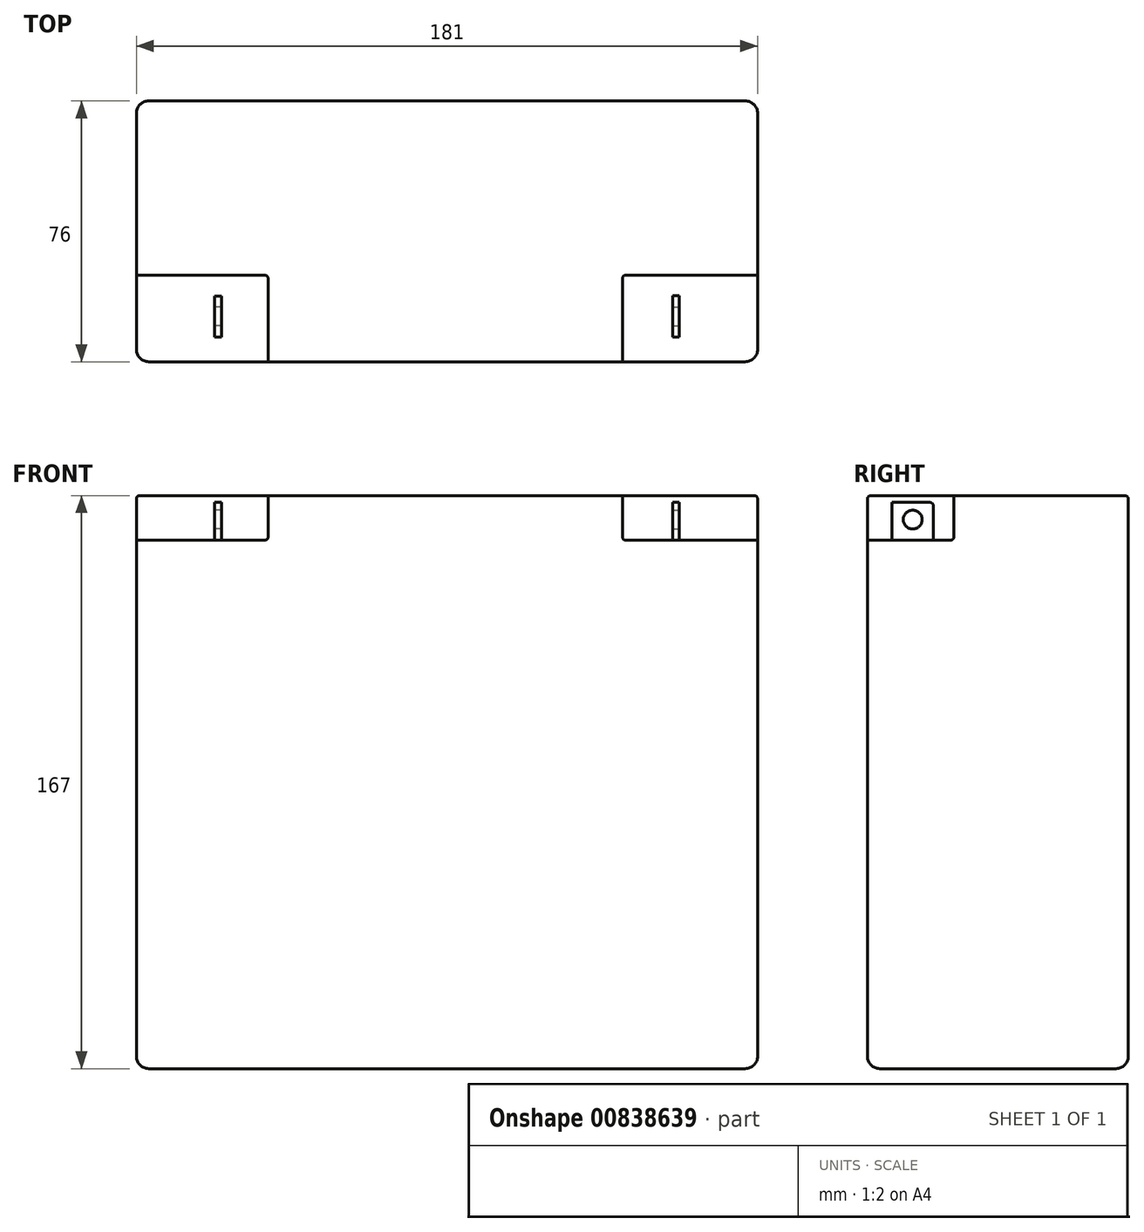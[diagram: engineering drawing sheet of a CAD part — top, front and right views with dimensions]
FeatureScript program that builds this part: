
annotation { "Feature Type Name" : "Feature", "Feature Type Description" : "" }
export const myFeature = defineFeature(function(context is Context, id is Id, definition is map)
    precondition{}
    {
        {
            var Q0;
            Q0=qCreatedBy(makeId("Top.planeOp"),FACE);
            var sketch = newSketch(context, id + "F0", { "sketchPlane" : qUnion([Q0])});
            skLineSegment(sketch, "E0.bottom", {"start": v(-83.93, 37.81) * mm, "end": v(97.07, 37.81) * mm});
            skLineSegment(sketch, "E0.top", {"start": v(-83.93, -38.19) * mm, "end": v(97.07, -38.19) * mm});
            skLineSegment(sketch, "E0.left", {"start": v(-83.93, 37.81) * mm, "end": v(-83.93, -38.19) * mm});
            skLineSegment(sketch, "E0.right", {"start": v(97.07, 37.81) * mm, "end": v(97.07, -38.19) * mm});
            skSolve(sketch);
        }
        {
            var Q0;
            Q0=makeQuery(id+"F0.imprint","IMPRINT",FACE,{"disambiguationData":[TD([[makeQuery(id+"F0.imprint","IMPRINT",EDGE,{"derivedFrom":sQuery(id+"F0.wireOp",EDGE,"E0.bottom")}),-1.0]])]});
            extrude(context, id + "F1", {"entities" : qUnion([Q0]), "depth" : 167 * mm, "offsetDistance" : 25.4 * mm});
        }
        {
            var Q0;
            Q0=makeQuery(id+"F1.opExtrude","SWEPT_FACE",FACE,{"disambiguationData":[OSD([sQuery(id+"F0.wireOp",EDGE,"E0.right")])]});
            var sketch = newSketch(context, id + "F2", { "sketchPlane" : qUnion([Q0])});
            skLineSegment(sketch, "E1.bottom", {"start": v(-38.19, 167) * mm, "end": v(-12.99, 167) * mm});
            skLineSegment(sketch, "E1.top", {"start": v(-38.19, 154) * mm, "end": v(-12.99, 154) * mm});
            skLineSegment(sketch, "E1.left", {"start": v(-38.19, 167) * mm, "end": v(-38.19, 154) * mm});
            skLineSegment(sketch, "E1.right", {"start": v(-12.99, 167) * mm, "end": v(-12.99, 154) * mm});
            skSolve(sketch);
        }
        {
            var Q0;
            Q0 = qSketchRegion(id + "F2", true);
            extrude(context, id + "F3", {"entities" : qUnion([Q0]), "operationType" : NewBodyOperationType.REMOVE, "oppositeDirection" : true, "depth" : 39.4 * mm, "offsetDistance" : 25.4 * mm});
        }
        {
            var Q0;
            Q0=makeQuery(id+"F1.opExtrude","SWEPT_FACE",FACE,{"disambiguationData":[OSD([sQuery(id+"F0.wireOp",EDGE,"E0.left")])]});
            var sketch = newSketch(context, id + "F4", { "sketchPlane" : qUnion([Q0])});
            skLineSegment(sketch, "E2.bottom", {"start": v(38.19, 167) * mm, "end": v(12.99, 167) * mm});
            skLineSegment(sketch, "E2.top", {"start": v(38.19, 154) * mm, "end": v(12.99, 154) * mm});
            skLineSegment(sketch, "E2.left", {"start": v(38.19, 167) * mm, "end": v(38.19, 154) * mm});
            skLineSegment(sketch, "E2.right", {"start": v(12.99, 167) * mm, "end": v(12.99, 154) * mm});
            skSolve(sketch);
        }
        {
            var Q0;
            Q0 = qSketchRegion(id + "F4", true);
            extrude(context, id + "F5", {"entities" : qUnion([Q0]), "operationType" : NewBodyOperationType.REMOVE, "oppositeDirection" : true, "depth" : 38.4 * mm, "offsetDistance" : 25.4 * mm});
        }
        {
            var Q0;
            Q0=makeQuery(id+"F3.boolean.opBoolean","COPY",FACE,{"derivedFrom":makeQuery(id+"F3.opExtrude","SWEPT_FACE",FACE,{"disambiguationData":[OSD([sQuery(id+"F2.wireOp",EDGE,"E1.top")])]})});
            var sketch = newSketch(context, id + "F6", { "sketchPlane" : qUnion([Q0])});
            skLineSegment(sketch, "E3.top", {"start": v(74.27, -30.99) * mm, "end": v(72.14, -30.99) * mm});
            skLineSegment(sketch, "E4.bottom", {"start": v(74.27, -30.99) * mm, "end": v(72.27, -30.99) * mm});
            skLineSegment(sketch, "E4.top", {"start": v(74.27, -18.99) * mm, "end": v(72.27, -18.99) * mm});
            skLineSegment(sketch, "E4.left", {"start": v(74.27, -30.99) * mm, "end": v(74.27, -18.99) * mm});
            skLineSegment(sketch, "E4.right", {"start": v(72.27, -30.99) * mm, "end": v(72.27, -18.99) * mm});
            skSolve(sketch);
        }
        {
            var Q0;
            Q0 = qSketchRegion(id + "F6", true);
            extrude(context, id + "F7", {"entities" : qUnion([Q0]), "operationType" : NewBodyOperationType.ADD, "depth" : 11 * mm, "offsetDistance" : 25.4 * mm});
        }
        {
            var Q0;
            Q0=makeQuery(id+"F7.opExtrude","CAP_EDGE",EDGE,{"disambiguationData":[OSD([sQuery(id+"F6.wireOp",EDGE,"E4.bottom")])],"isStart":false});
            var Q1;
            Q1=makeQuery(id+"F7.opExtrude","CAP_EDGE",EDGE,{"disambiguationData":[OSD([sQuery(id+"F6.wireOp",EDGE,"E4.top")])],"isStart":false});
            fillet(context, id + "F8", {"entities" : qUnion([Q0, Q1]), "radius" : 1 * mm, "tangentPropagation" : true, "allowEdgeOverflow" : false});
        }
        {
            var Q0;
            Q0=makeQuery(id+"F7.opExtrude","SWEPT_FACE",FACE,{"disambiguationData":[OSD([sQuery(id+"F6.wireOp",EDGE,"E4.left")])]});
            var sketch = newSketch(context, id + "F9", { "sketchPlane" : qUnion([Q0])});
            skCircle(sketch, "E5", {"center": v(-24.99, 160) * mm, "radius": 2.75 * mm});
            skPoint(sketch, "E5.centerSnap0", {"position": v(-24.99, 165) * mm});
            skSolve(sketch);
        }
        {
            var Q0;
            Q0 = qSketchRegion(id + "F9", true);
            extrude(context, id + "F10", {"entities" : qUnion([Q0]), "operationType" : NewBodyOperationType.REMOVE, "oppositeDirection" : true, "depth" : 3 * mm, "offsetDistance" : 25.4 * mm});
        }
        {
            var Q0;
            Q0=makeQuery(id+"F5.boolean.opBoolean","COPY",FACE,{"derivedFrom":makeQuery(id+"F5.opExtrude","SWEPT_FACE",FACE,{"disambiguationData":[OSD([sQuery(id+"F4.wireOp",EDGE,"E2.top")])]})});
            var sketch = newSketch(context, id + "F11", { "sketchPlane" : qUnion([Q0])});
            skLineSegment(sketch, "E6.bottom", {"start": v(-61.12, -31) * mm, "end": v(-59.12, -31) * mm});
            skLineSegment(sketch, "E6.top", {"start": v(-61.12, -19) * mm, "end": v(-59.12, -19) * mm});
            skLineSegment(sketch, "E6.left", {"start": v(-61.12, -31) * mm, "end": v(-61.12, -19) * mm});
            skLineSegment(sketch, "E6.right", {"start": v(-59.12, -31) * mm, "end": v(-59.12, -19) * mm});
            skSolve(sketch);
        }
        {
            var Q0;
            Q0=makeQuery(id+"F11.imprint","IMPRINT",FACE,{"disambiguationData":[TD([[makeQuery(id+"F11.imprint","IMPRINT",EDGE,{"derivedFrom":sQuery(id+"F11.wireOp",EDGE,"E6.bottom")}),1.0]])]});
            extrude(context, id + "F12", {"entities" : qUnion([Q0]), "operationType" : NewBodyOperationType.ADD, "depth" : 11 * mm, "offsetDistance" : 25.4 * mm});
        }
        {
            var Q0;
            Q0=makeQuery(id+"F12.opExtrude","CAP_EDGE",EDGE,{"disambiguationData":[OSD([sQuery(id+"F11.wireOp",EDGE,"E6.bottom")])],"isStart":false});
            var Q1;
            Q1=makeQuery(id+"F12.opExtrude","CAP_EDGE",EDGE,{"disambiguationData":[OSD([sQuery(id+"F11.wireOp",EDGE,"E6.top")])],"isStart":false});
            fillet(context, id + "F13", {"entities" : qUnion([Q0, Q1]), "radius" : 1 * mm, "tangentPropagation" : true, "allowEdgeOverflow" : false});
        }
        {
            var Q0;
            Q0=makeQuery(id+"F12.opExtrude","SWEPT_FACE",FACE,{"disambiguationData":[OSD([sQuery(id+"F11.wireOp",EDGE,"E6.left")])]});
            var sketch = newSketch(context, id + "F14", { "sketchPlane" : qUnion([Q0])});
            skCircle(sketch, "E7", {"center": v(25, 160) * mm, "radius": 2.75 * mm});
            skPoint(sketch, "E7.centerSnap0", {"position": v(25, 165) * mm});
            skSolve(sketch);
        }
        {
            var Q0;
            Q0 = qSketchRegion(id + "F14", true);
            extrude(context, id + "F15", {"entities" : qUnion([Q0]), "operationType" : NewBodyOperationType.REMOVE, "oppositeDirection" : true, "depth" : 3 * mm, "offsetDistance" : 25.4 * mm});
        }
        {
            var Q0;
            Q0=makeQuery(id+"F1.opExtrude","SWEPT_EDGE",EDGE,{"disambiguationData":[OSD([sQuery(id+"F0.wireOp",EDGE,"E0.top"),sQuery(id+"F0.wireOp",EDGE,"E0.right")])]});
            var Q1;
            Q1=makeQuery(id+"F1.opExtrude","CAP_EDGE",EDGE,{"disambiguationData":[OSD([sQuery(id+"F0.wireOp",EDGE,"E0.right")])],"isStart":true});
            var Q2;
            Q2=makeQuery(id+"F1.opExtrude","SWEPT_EDGE",EDGE,{"disambiguationData":[OSD([sQuery(id+"F0.wireOp",EDGE,"E0.bottom"),sQuery(id+"F0.wireOp",EDGE,"E0.right")])]});
            var Q3;
            Q3=makeQuery(id+"F1.opExtrude","CAP_EDGE",EDGE,{"disambiguationData":[OSD([sQuery(id+"F0.wireOp",EDGE,"E0.bottom")])],"isStart":true});
            var Q4;
            Q4=makeQuery(id+"F1.opExtrude","CAP_EDGE",EDGE,{"disambiguationData":[OSD([sQuery(id+"F0.wireOp",EDGE,"E0.top")])],"isStart":true});
            var Q5;
            Q5=makeQuery(id+"F1.opExtrude","SWEPT_EDGE",EDGE,{"disambiguationData":[OSD([sQuery(id+"F0.wireOp",EDGE,"E0.bottom"),sQuery(id+"F0.wireOp",EDGE,"E0.left")])]});
            var Q6;
            Q6=makeQuery(id+"F1.opExtrude","CAP_EDGE",EDGE,{"disambiguationData":[OSD([sQuery(id+"F0.wireOp",EDGE,"E0.left")])],"isStart":true});
            var Q7;
            Q7=makeQuery(id+"F1.opExtrude","SWEPT_EDGE",EDGE,{"disambiguationData":[OSD([sQuery(id+"F0.wireOp",EDGE,"E0.top"),sQuery(id+"F0.wireOp",EDGE,"E0.left")])]});
            fillet(context, id + "F16", {"entities" : qUnion([Q0, Q1, Q2, Q3, Q4, Q5, Q6, Q7]), "radius" : 3.6 * mm, "tangentPropagation" : true, "allowEdgeOverflow" : false});
        }
        {
            var Q0;
            Q0=makeQuery(id+"F5.boolean.opBoolean","COPY",EDGE,{"derivedFrom":makeQuery(id+"F5.opExtrude","SWEPT_EDGE",EDGE,{"disambiguationData":[OSD([sQuery(id+"F0.wireOp",EDGE,"E0.top"),sQuery(id+"F0.wireOp",EDGE,"E0.left"),sQuery(id+"F4.wireOp",EDGE,"E2.top"),sQuery(id+"F4.wireOp",EDGE,"E2.left")])]})});
            var Q1;
            Q1=makeQuery(id+"F5.boolean.opBoolean","COPY",EDGE,{"derivedFrom":makeQuery(id+"F5.opExtrude","CAP_EDGE",EDGE,{"disambiguationData":[OSD([sQuery(id+"F4.wireOp",EDGE,"E2.top")])],"isStart":true})});
            var Q2;
            Q2=makeQuery(id+"F5.boolean.opBoolean","COPY",EDGE,{"derivedFrom":makeQuery(id+"F5.opExtrude","CAP_EDGE",EDGE,{"disambiguationData":[OSD([sQuery(id+"F4.wireOp",EDGE,"E2.right")])],"isStart":true})});
            var Q3;
            Q3=makeQuery(id+"F5.boolean.opBoolean","COPY",EDGE,{"derivedFrom":makeQuery(id+"F5.opExtrude","SWEPT_EDGE",EDGE,{"disambiguationData":[OSD([sQuery(id+"F0.wireOp",EDGE,"E0.left"),sQuery(id+"F4.wireOp",EDGE,"E2.bottom"),sQuery(id+"F4.wireOp",EDGE,"E2.right")])]})});
            var Q4;
            Q4=makeQuery(id+"F5.boolean.opBoolean","COPY",EDGE,{"derivedFrom":makeQuery(id+"F5.opExtrude","CAP_EDGE",EDGE,{"disambiguationData":[OSD([sQuery(id+"F4.wireOp",EDGE,"E2.bottom")])],"isStart":false})});
            var Q5;
            Q5=makeQuery(id+"F5.boolean.opBoolean","COPY",EDGE,{"derivedFrom":makeQuery(id+"F5.opExtrude","CAP_EDGE",EDGE,{"disambiguationData":[OSD([sQuery(id+"F4.wireOp",EDGE,"E2.right")])],"isStart":false})});
            var Q6;
            Q6=makeQuery(id+"F5.boolean.opBoolean","COPY",EDGE,{"derivedFrom":makeQuery(id+"F5.opExtrude","CAP_EDGE",EDGE,{"disambiguationData":[OSD([sQuery(id+"F4.wireOp",EDGE,"E2.top")])],"isStart":false})});
            var Q7;
            Q7=makeQuery(id+"F5.boolean.opBoolean","COPY",EDGE,{"derivedFrom":makeQuery(id+"F5.opExtrude","SWEPT_EDGE",EDGE,{"disambiguationData":[OSD([sQuery(id+"F4.wireOp",EDGE,"E2.top"),sQuery(id+"F4.wireOp",EDGE,"E2.right")])]})});
            var Q8;
            Q8=makeQuery(id+"F5.boolean.opBoolean","COPY",EDGE,{"derivedFrom":makeQuery(id+"F5.opExtrude","CAP_EDGE",EDGE,{"disambiguationData":[OSD([sQuery(id+"F4.wireOp",EDGE,"E2.left")])],"isStart":false})});
            var Q9;
            Q9=makeQuery(id+"F1.opExtrude","CAP_EDGE",EDGE,{"disambiguationData":[OSD([sQuery(id+"F0.wireOp",EDGE,"E0.top")])],"isStart":false});
            var Q10;
            Q10=makeQuery(id+"F1.opExtrude","CAP_EDGE",EDGE,{"disambiguationData":[OSD([sQuery(id+"F0.wireOp",EDGE,"E0.left")])],"isStart":false});
            var Q11;
            Q11=makeQuery(id+"F3.boolean.opBoolean","COPY",EDGE,{"derivedFrom":makeQuery(id+"F3.opExtrude","SWEPT_EDGE",EDGE,{"disambiguationData":[OSD([sQuery(id+"F0.wireOp",EDGE,"E0.right"),sQuery(id+"F2.wireOp",EDGE,"E1.bottom"),sQuery(id+"F2.wireOp",EDGE,"E1.right")])]})});
            var Q12;
            Q12=makeQuery(id+"F3.boolean.opBoolean","COPY",EDGE,{"derivedFrom":makeQuery(id+"F3.opExtrude","CAP_EDGE",EDGE,{"disambiguationData":[OSD([sQuery(id+"F2.wireOp",EDGE,"E1.bottom")])],"isStart":false})});
            var Q13;
            Q13=makeQuery(id+"F3.boolean.opBoolean","COPY",EDGE,{"derivedFrom":makeQuery(id+"F3.opExtrude","CAP_EDGE",EDGE,{"disambiguationData":[OSD([sQuery(id+"F2.wireOp",EDGE,"E1.right")])],"isStart":false})});
            var Q14;
            Q14=makeQuery(id+"F3.boolean.opBoolean","COPY",EDGE,{"derivedFrom":makeQuery(id+"F3.opExtrude","SWEPT_EDGE",EDGE,{"disambiguationData":[OSD([sQuery(id+"F2.wireOp",EDGE,"E1.top"),sQuery(id+"F2.wireOp",EDGE,"E1.right")])]})});
            var Q15;
            Q15=makeQuery(id+"F3.boolean.opBoolean","COPY",EDGE,{"derivedFrom":makeQuery(id+"F3.opExtrude","CAP_EDGE",EDGE,{"disambiguationData":[OSD([sQuery(id+"F2.wireOp",EDGE,"E1.top")])],"isStart":false})});
            var Q16;
            Q16=makeQuery(id+"F3.boolean.opBoolean","COPY",EDGE,{"derivedFrom":makeQuery(id+"F3.opExtrude","CAP_EDGE",EDGE,{"disambiguationData":[OSD([sQuery(id+"F2.wireOp",EDGE,"E1.left")])],"isStart":false})});
            var Q17;
            Q17=makeQuery(id+"F3.boolean.opBoolean","COPY",EDGE,{"derivedFrom":makeQuery(id+"F3.opExtrude","SWEPT_EDGE",EDGE,{"disambiguationData":[OSD([sQuery(id+"F0.wireOp",EDGE,"E0.top"),sQuery(id+"F0.wireOp",EDGE,"E0.right"),sQuery(id+"F2.wireOp",EDGE,"E1.top"),sQuery(id+"F2.wireOp",EDGE,"E1.left")])]})});
            var Q18;
            Q18=makeQuery(id+"F3.boolean.opBoolean","COPY",EDGE,{"derivedFrom":makeQuery(id+"F3.opExtrude","CAP_EDGE",EDGE,{"disambiguationData":[OSD([sQuery(id+"F2.wireOp",EDGE,"E1.right")])],"isStart":true})});
            var Q19;
            Q19=makeQuery(id+"F3.boolean.opBoolean","COPY",EDGE,{"derivedFrom":makeQuery(id+"F3.opExtrude","CAP_EDGE",EDGE,{"disambiguationData":[OSD([sQuery(id+"F2.wireOp",EDGE,"E1.top")])],"isStart":true})});
            fillet(context, id + "F17", {"entities" : qUnion([Q0, Q1, Q2, Q3, Q4, Q5, Q6, Q7, Q8, Q9, Q10, Q11, Q12, Q13, Q14, Q15, Q16, Q17, Q18, Q19]), "radius" : 1 * mm, "tangentPropagation" : true, "allowEdgeOverflow" : false});
        }
    });
